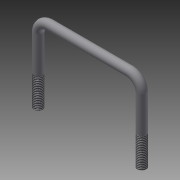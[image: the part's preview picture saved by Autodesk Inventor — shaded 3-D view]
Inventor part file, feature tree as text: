
AUTODESK INVENTOR PART (.ipt)
format: ipt  version: 2015 SP1 (Build 190203100, 203)  size: 97,792 bytes
history: native  units: in
note: dims shown in document units (in); Inventor stores cm internally (conversion verified against a paired STEP export)
features: thread x2, sketch x2, sweep x1
ambient origin geometry x8: Origin, YZ Plane, XZ Plane, XY Plane, X Axis, Y Axis, Z Axis, Center Point
bodies: Solid1 (feature_tree)
feature tree (5):
  sweep  "Sweep1"
  thread  "Thread1"  [1 undecoded]
  thread  "Thread2"  [1 undecoded]
  sketch  "Sketch1"  dims[d0=3.25in d1=4.375in d2=3.25in d3=0.375in]
  sketch  "Sketch2"  dims[d4=0.5in d5=0.0in d6=0.0in d7=1.25in d8=1.5in d9=1.25in d10=1.5in]
note: 2 required parameter values undecoded (feature->parameter linkage not recoverable at this tier; creation-order binding heuristic only, values carry confidence <= 0.55)
